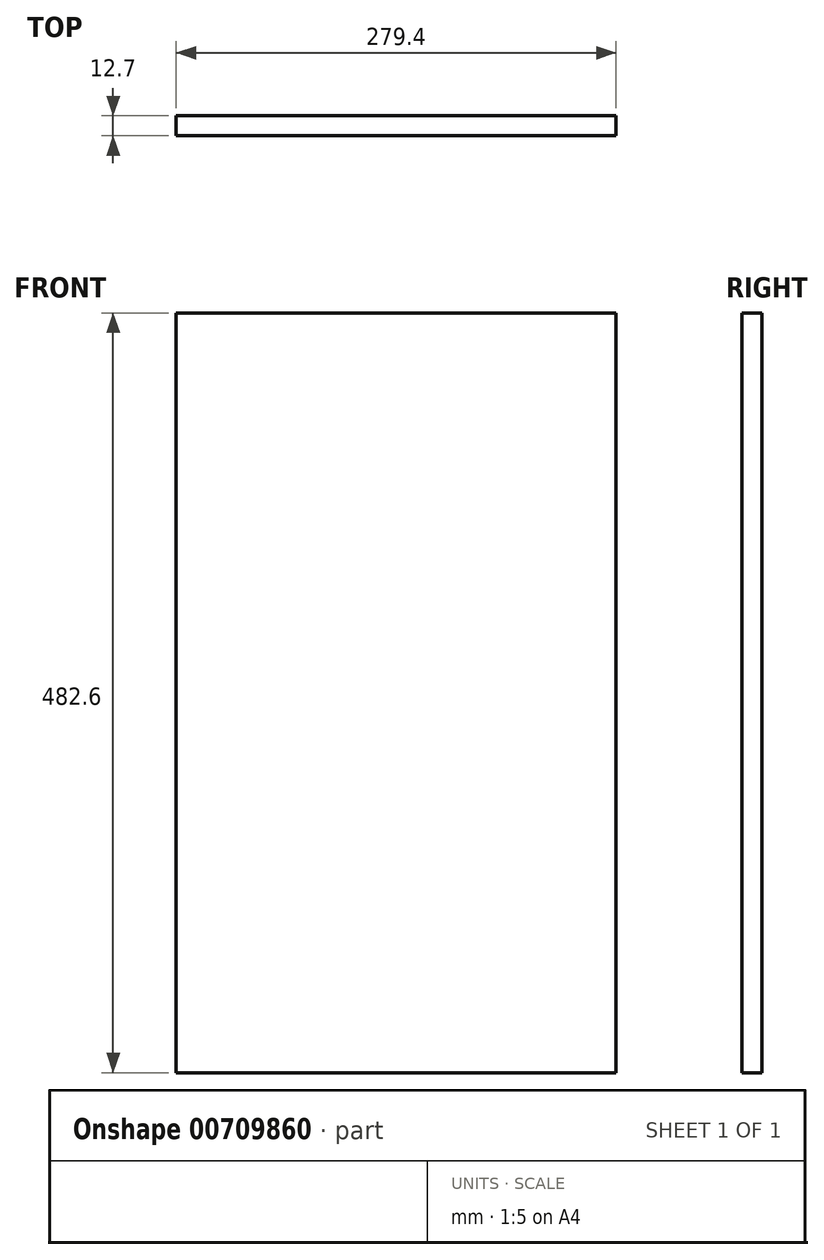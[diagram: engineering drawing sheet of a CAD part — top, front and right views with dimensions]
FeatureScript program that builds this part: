
annotation { "Feature Type Name" : "Feature", "Feature Type Description" : "" }
export const myFeature = defineFeature(function(context is Context, id is Id, definition is map)
    precondition{}
    {
        {
            var Q0;
            Q0=qCreatedBy(makeId("Front.planeOp"),FACE);
            var sketch = newSketch(context, id + "F0", { "sketchPlane" : qUnion([Q0])});
            skLineSegment(sketch, "E0.bottom", {"start": v(-132, 235.26) * mm, "end": v(147.4, 235.26) * mm});
            skLineSegment(sketch, "E0.top", {"start": v(-132, -247.34) * mm, "end": v(147.4, -247.34) * mm});
            skLineSegment(sketch, "E0.left", {"start": v(-132, 235.26) * mm, "end": v(-132, -247.34) * mm});
            skLineSegment(sketch, "E0.right", {"start": v(147.4, 235.26) * mm, "end": v(147.4, -247.34) * mm});
            skSolve(sketch);
        }
        {
            var Q0;
            Q0=makeQuery(id+"F0.imprint","IMPRINT",FACE,{"disambiguationData":[TD([[makeQuery(id+"F0.imprint","IMPRINT",EDGE,{"derivedFrom":sQuery(id+"F0.wireOp",EDGE,"E0.bottom")}),-1.0]])]});
            extrude(context, id + "F1", {"entities" : qUnion([Q0]), "depth" : 12.7 * mm, "offsetDistance" : 25.4 * mm});
        }
    });
